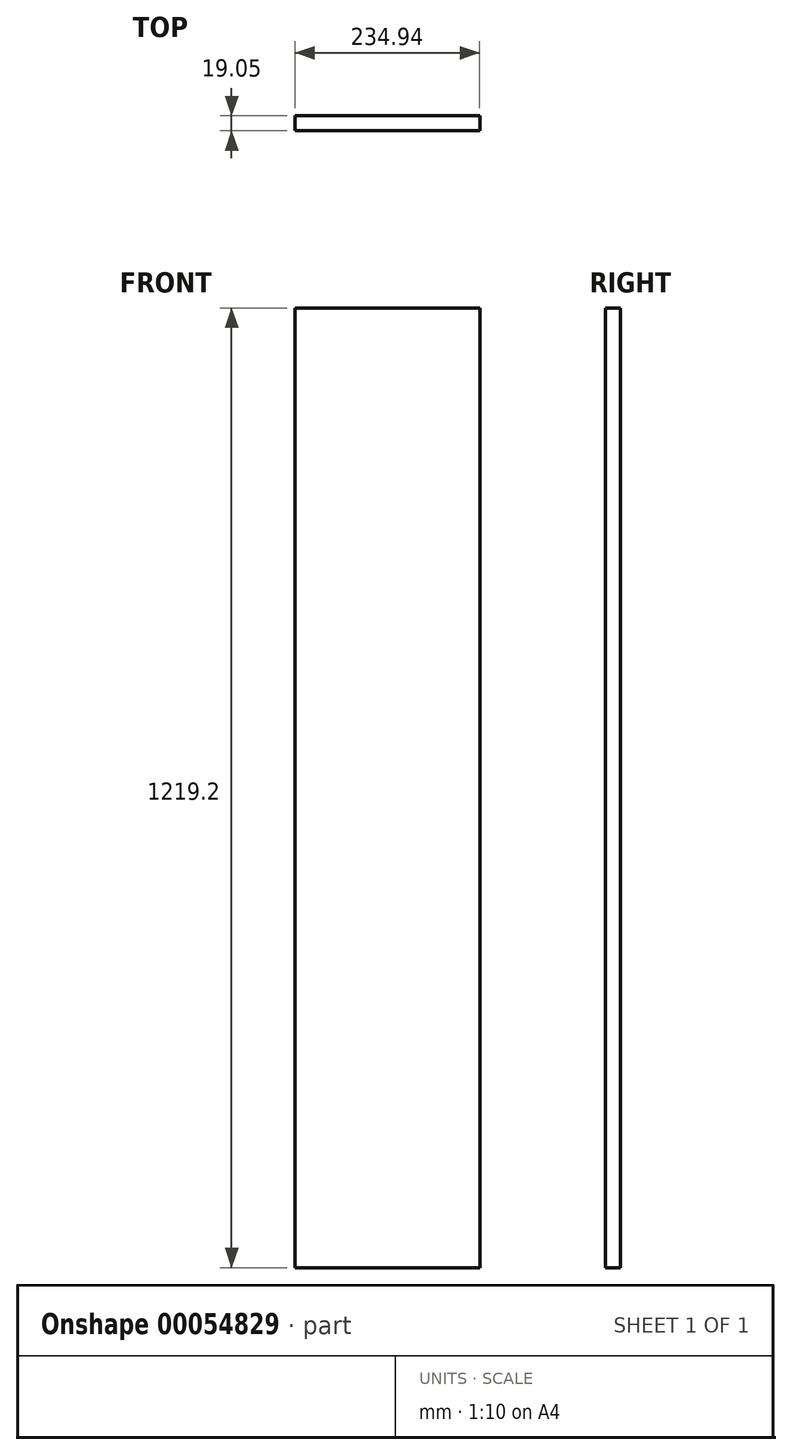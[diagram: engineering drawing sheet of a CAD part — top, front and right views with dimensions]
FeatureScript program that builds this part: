
annotation { "Feature Type Name" : "Feature", "Feature Type Description" : "" }
export const myFeature = defineFeature(function(context is Context, id is Id, definition is map)
    precondition{}
    {
        {
            var Q0;
            Q0=qCreatedBy(makeId("Front.planeOp"),FACE);
            var sketch = newSketch(context, id + "F0", { "sketchPlane" : qUnion([Q0])});
            skLineSegment(sketch, "E0.rect.bottom", {"start": v(-117.47, 599.2) * mm, "end": v(117.48, 599.2) * mm});
            skLineSegment(sketch, "E0.rect.top", {"start": v(-117.48, -620) * mm, "end": v(117.47, -620) * mm});
            skLineSegment(sketch, "E0.rect.left", {"start": v(-117.47, 599.2) * mm, "end": v(-117.48, -620) * mm});
            skLineSegment(sketch, "E0.rect.right", {"start": v(117.48, 599.2) * mm, "end": v(117.47, -620) * mm});
            skPoint(sketch, "E0.rect.middle", {"position": v(0, -10.4) * mm});
            skSolve(sketch);
        }
        {
            var Q0;
            Q0 = qSketchRegion(id + "F0", true);
            extrude(context, id + "F1", {"entities" : qUnion([Q0]), "depth" : 19.05 * mm});
        }
    });
